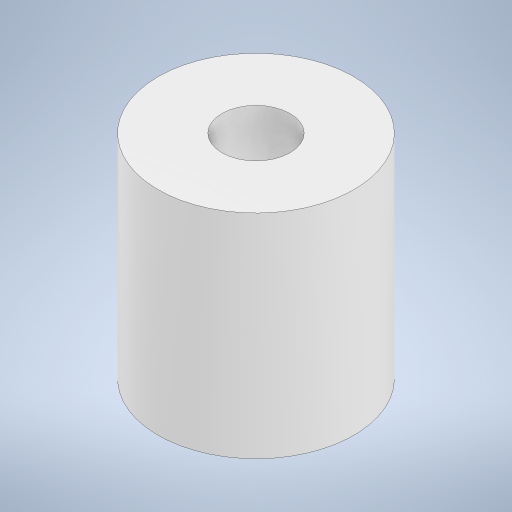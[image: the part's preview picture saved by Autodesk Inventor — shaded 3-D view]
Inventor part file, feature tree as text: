
AUTODESK INVENTOR PART (.ipt)
format: ipt  version: 2024 (Build 280153000, 153)  size: 202,752 bytes
history: native  units: in
note: dims shown in document units (in); Inventor stores cm internally (conversion verified against a paired STEP export)
features: extrude x1, sketch x1
ambient origin geometry x8: Origin, YZ Plane, XZ Plane, XY Plane, X Axis, Y Axis, Z Axis, Center Point
bodies: Solid1 (feature_tree)
feature tree (2):
  extrude  "Extrusion1"  Depth=0.625in
  sketch  "Sketch1"  dims[d0=0.2in d1=0.1875in d2=0.625in d3=0.0in]
